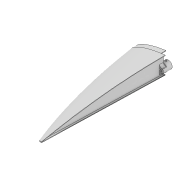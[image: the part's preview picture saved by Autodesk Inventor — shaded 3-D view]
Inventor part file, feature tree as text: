
AUTODESK INVENTOR PART (.ipt)
format: ipt  version: 2022 (Build 260153000, 153)  size: 911,872 bytes
history: native  units: mm
features: sketch x9, extrude x8, plane x4, projected_geometry x2, loft x1, shell x1, fillet x1, mirror x1
ambient origin geometry x8: Origin, YZ Plane, XZ Plane, XY Plane, X Axis, Y Axis, Z Axis, Center Point
bodies: Solid5 (feature_tree)
feature tree (27):
  plane  "Work Plane7"
  sketch  "Sketch3"  dims[d45=-250.0mm d46=70.0mm d47=1.0mm d48=5.0mm]
  plane  "Work Plane6"
  sketch  "Sketch17"  dims[d68=0.0mm d69=90.0deg d70=0.0mm d71=90.0deg]
  sketch  "Sketch18"  dims[d72=0.0mm d73=90.0deg d74=0.0mm d75=90.0deg]
  plane  "Work Plane8"
  loft  "Loft4"
  shell  "Shell3"  Thickness=5.0mm
  plane  "Work Plane10"
  sketch  "Sketch32"  dims[d104=66.0mm d122=0.5mm d123=0.0mm]
  extrude  "Extrusion19"  TaperAngle=0.0deg  [1 undecoded]
  extrude  "Extrusion20"  TaperAngle=0.0deg  [1 undecoded]
  sketch  "Sketch36"  dims[d124=0.5mm d125=0.0mm d135=9.8mm]
  extrude  "Extrusion24"  Depth=1.0mm
  extrude  "Extrusion25"  Depth=0.5mm TaperAngle=0.0deg
  extrude  "Extrusion26"  Depth=9.8mm
  extrude  "Extrusion27"  Depth=12.2mm
  extrude  "Extrusion28"  Depth=1.0mm TaperAngle=0.0deg
  fillet  "Fillet4"  Radius=1.5mm
  extrude  "Extrusion31"  Depth=10.0mm TaperAngle=0.0deg
  mirror  "Mirror1"
  sketch  "Sketch19"  dims[d76=0.0mm d77=90.0deg d78=1.0mm]
  sketch  "Sketch37"  dims[d136=4.15mm d137=12.2mm]
  sketch  "Sketch38"  dims[d138=2.0mm d139=1.0mm d140=0.0mm d141=1.5mm]
  sketch  "Sketch41"  dims[d142=12.0mm d143=0.0mm d144=10.0mm d145=0.0mm d146=2.1mm d147=6.0mm d148=100.0mm d149=0.0mm d152=8.0mm d153=0.0mm d154=5.0mm d158=2.3mm d159=4.3mm d160=1.15mm d170=3.0mm d171=3.0mm d172=40.0mm d173=1.0mm d174=4.0mm d175=10.0mm d176=0.0mm]
  projected_geometry  "Projected Loop14"
  projected_geometry  "Project Cut Edges5"
note: 2 required parameter values undecoded (feature->parameter linkage not recoverable at this tier; creation-order binding heuristic only, values carry confidence <= 0.55)
